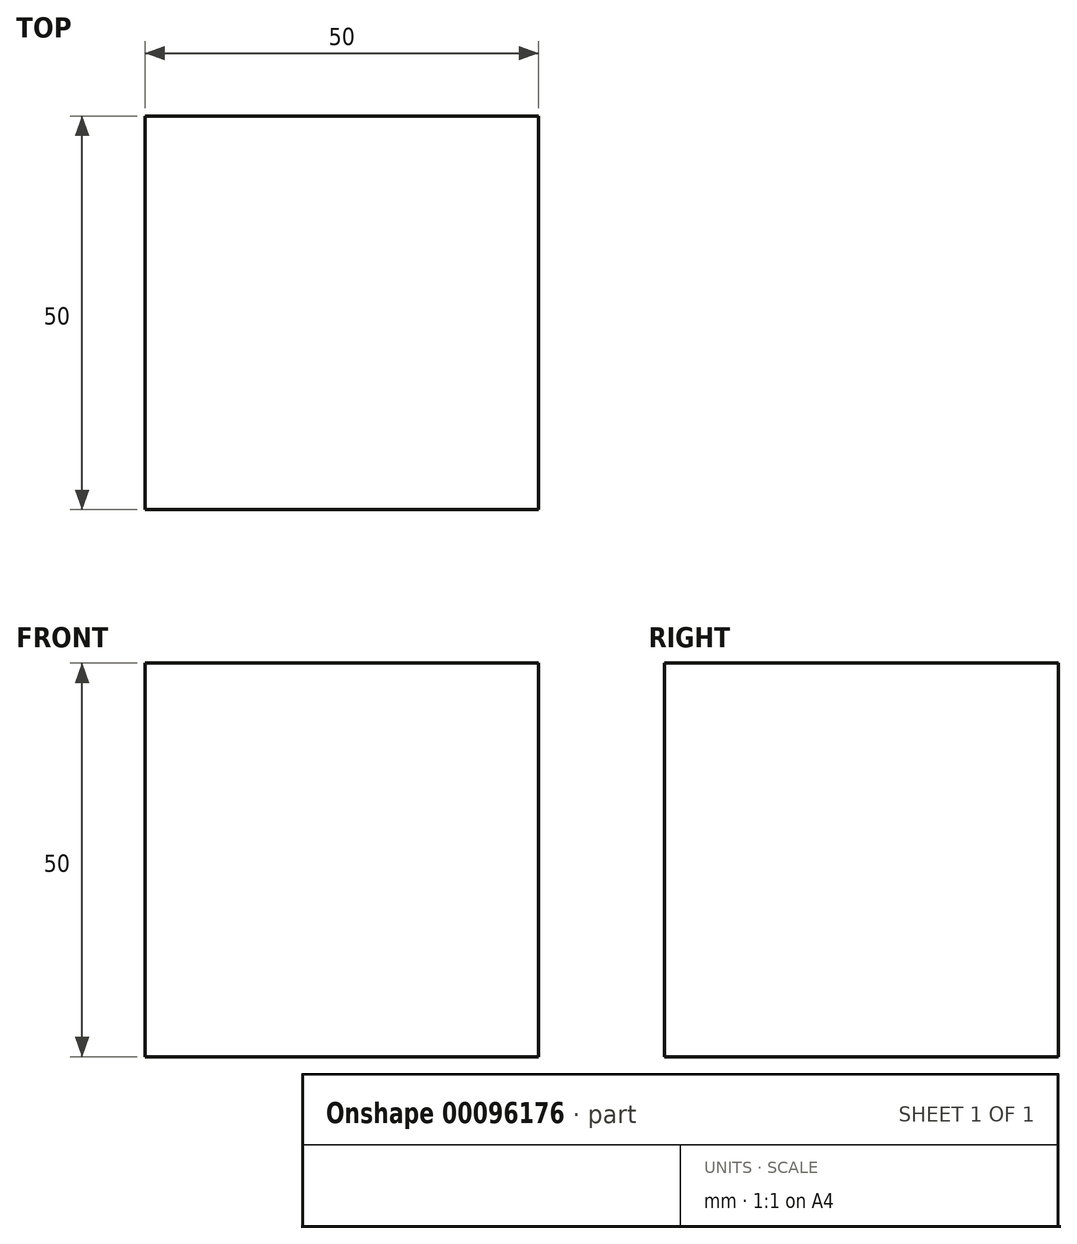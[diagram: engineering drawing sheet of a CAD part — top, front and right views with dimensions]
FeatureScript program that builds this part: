
annotation { "Feature Type Name" : "Feature", "Feature Type Description" : "" }
export const myFeature = defineFeature(function(context is Context, id is Id, definition is map)
    precondition{}
    {
        {
            var Q0;
            Q0=qCreatedBy(makeId("Front.planeOp"),FACE);
            var sketch = newSketch(context, id + "F0", { "sketchPlane" : qUnion([Q0])});
            skLineSegment(sketch, "E0.bottom", {"start": v(25, -25) * mm, "end": v(-25, -25) * mm});
            skLineSegment(sketch, "E0.top", {"start": v(25, 25) * mm, "end": v(-25, 25) * mm});
            skLineSegment(sketch, "E0.left", {"start": v(25, -25) * mm, "end": v(25, 25) * mm});
            skLineSegment(sketch, "E0.right", {"start": v(-25, -25) * mm, "end": v(-25, 25) * mm});
            skPoint(sketch, "E0.middle", {"position": v(0, 0) * mm});
            skSolve(sketch);
        }
        {
            var Q0;
            Q0=makeQuery(id+"F0.imprint","IMPRINT",FACE,{"disambiguationData":[TD([[makeQuery(id+"F0.imprint","IMPRINT",EDGE,{"derivedFrom":sQuery(id+"F0.wireOp",EDGE,"E0.bottom")}),-1.0]])]});
            extrude(context, id + "F1", {"entities" : qUnion([Q0]), "depth" : 50 * mm});
        }
    });
